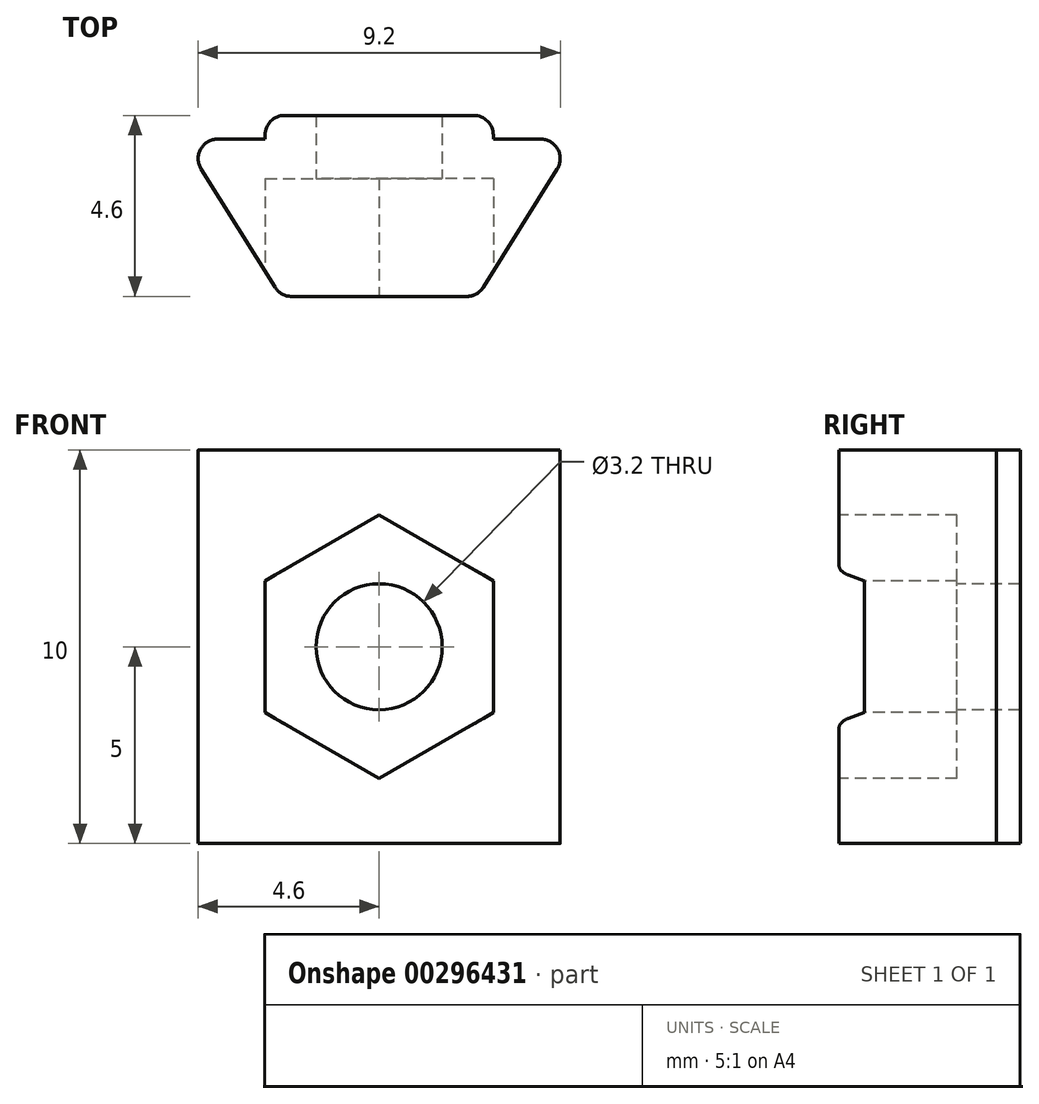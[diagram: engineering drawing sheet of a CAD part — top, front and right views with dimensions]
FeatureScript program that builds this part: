
annotation { "Feature Type Name" : "Feature", "Feature Type Description" : "" }
export const myFeature = defineFeature(function(context is Context, id is Id, definition is map)
    precondition{}
    {
        {
            var Q0;
            Q0=qCreatedBy(makeId("Top.planeOp"),FACE);
            var sketch = newSketch(context, id + "F0", { "sketchPlane" : qUnion([Q0])});
            skLineSegment(sketch, "E0.bottom", {"start": v(5, -2) * mm, "end": v(-5, -2) * mm, "construction": true});
            skLineSegment(sketch, "E0.top", {"start": v(5, 2) * mm, "end": v(-5, 2) * mm, "construction": true});
            skLineSegment(sketch, "E0.left", {"start": v(5, -2) * mm, "end": v(5, 2) * mm, "construction": true});
            skLineSegment(sketch, "E0.right", {"start": v(-5, -2) * mm, "end": v(-5, 2) * mm, "construction": true});
            skPoint(sketch, "E0.middle", {"position": v(0, 0) * mm});
            skLineSegment(sketch, "E1.bottom", {"start": v(2.9, 2.6) * mm, "end": v(-2.9, 2.6) * mm, "construction": true});
            skLineSegment(sketch, "E1.top", {"start": v(2.9, 1.4) * mm, "end": v(-2.9, 1.4) * mm, "construction": true});
            skLineSegment(sketch, "E1.left", {"start": v(2.9, 2.6) * mm, "end": v(2.9, 1.4) * mm, "construction": true});
            skLineSegment(sketch, "E1.right", {"start": v(-2.9, 2.6) * mm, "end": v(-2.9, 1.4) * mm, "construction": true});
            skPoint(sketch, "E1.middle", {"position": v(0, 2) * mm});
            skLineSegment(sketch, "E2", {"start": v(-5, 2) * mm, "end": v(-2.5, -2) * mm});
            skLineSegment(sketch, "E3", {"start": v(5, 2) * mm, "end": v(2.5, -2) * mm});
            skLineSegment(sketch, "E4", {"start": v(-2.5, -2) * mm, "end": v(2.5, -2) * mm});
            skLineSegment(sketch, "E5", {"start": v(-5, 2) * mm, "end": v(-2.9, 2) * mm});
            skLineSegment(sketch, "E6", {"start": v(-2.9, 2) * mm, "end": v(-2.9, 2.6) * mm});
            skLineSegment(sketch, "E7", {"start": v(-2.9, 2.6) * mm, "end": v(2.9, 2.6) * mm});
            skLineSegment(sketch, "E8", {"start": v(2.9, 2.6) * mm, "end": v(2.9, 2) * mm});
            skLineSegment(sketch, "E9", {"start": v(2.9, 2) * mm, "end": v(5, 2) * mm});
            skSolve(sketch);
        }
        {
            var Q0;
            Q0 = qSketchRegion(id + "F0", true);
            extrude(context, id + "F1", {"entities" : qUnion([Q0]), "depth" : 10 * mm});
        }
        {
            var Q0;
            Q0=makeQuery(id+"F1.opExtrude","SWEPT_FACE",FACE,{"disambiguationData":[OSD([sQuery(id+"F0.wireOp",EDGE,"E4")])]});
            var sketch = newSketch(context, id + "F2", { "sketchPlane" : qUnion([Q0])});
            skCircle(sketch, "E10.cCircle", {"center": v(0, 5) * mm, "radius": 2.9 * mm, "construction": true});
            skPoint(sketch, "E10.cCircle.centerSnap0", {"position": v(2.5, 5) * mm});
            skPoint(sketch, "E10.cCircle.centerSnap1", {"position": v(0, 10) * mm});
            skLineSegment(sketch, "E10.0", {"start": v(2.9, 3.33) * mm, "end": v(0, 1.65) * mm});
            skLineSegment(sketch, "E10.1", {"start": v(0, 1.65) * mm, "end": v(-2.9, 3.33) * mm});
            skLineSegment(sketch, "E10.2", {"start": v(-2.9, 3.33) * mm, "end": v(-2.9, 6.67) * mm});
            skLineSegment(sketch, "E10.3", {"start": v(-2.9, 6.67) * mm, "end": v(0, 8.35) * mm});
            skLineSegment(sketch, "E10.4", {"start": v(0, 8.35) * mm, "end": v(2.9, 6.67) * mm});
            skLineSegment(sketch, "E10.5", {"start": v(2.9, 6.67) * mm, "end": v(2.9, 3.33) * mm});
            skPoint(sketch, "E10.0.midPoint", {"position": v(1.45, 2.49) * mm});
            skCircle(sketch, "E11", {"center": v(0, 5) * mm, "radius": 1.6 * mm});
            skSolve(sketch);
        }
        {
            var Q0;
            Q0=makeQuery(id+"F2.imprint","IMPRINT",FACE,{"disambiguationData":[TD([[makeQuery(id+"F2.imprint","IMPRINT",EDGE,{"derivedFrom":sQuery(id+"F2.wireOp",EDGE,"E11")}),1.0]])]});
            extrude(context, id + "F3", {"entities" : qUnion([Q0]), "operationType" : NewBodyOperationType.REMOVE, "endBound" : BoundingType.THROUGH_ALL, "oppositeDirection" : true, "depth" : 25 * mm});
        }
        {
            var Q0;
            Q0=makeQuery(id+"F2.imprint","IMPRINT",FACE,{"disambiguationData":[TD([[makeQuery(id+"F2.imprint","IMPRINT",EDGE,{"derivedFrom":sQuery(id+"F2.wireOp",EDGE,"E11")}),-1.0]])]});
            var Q1;
            {var subQ0=sQuery(id+"F2.wireOp",EDGE,"E10.5");Q1=makeQuery(id+"F2.imprint","IMPRINT",FACE,{"disambiguationData":[TD([[makeQuery(id+"F2.imprint","IMPRINT",EDGE,{"derivedFrom":subQ0}),-1.0]])]});}
            var Q2;
            {var subQ0=sQuery(id+"F2.wireOp",EDGE,"E10.2");Q2=makeQuery(id+"F2.imprint","IMPRINT",FACE,{"disambiguationData":[TD([[makeQuery(id+"F2.imprint","IMPRINT",EDGE,{"derivedFrom":subQ0}),-1.0]])]});}
            extrude(context, id + "F4", {"entities" : qUnion([Q0, Q1, Q2]), "operationType" : NewBodyOperationType.REMOVE, "oppositeDirection" : true, "depth" : 3 * mm});
        }
        {
            var Q0;
            Q0=makeQuery(id+"F1.opExtrude","SWEPT_EDGE",EDGE,{"disambiguationData":[OSD([sQuery(id+"F0.wireOp",EDGE,"E2"),sQuery(id+"F0.wireOp",EDGE,"E5")])]});
            var Q1;
            {var subQ0=sQuery(id+"F0.wireOp",EDGE,"E2");var subQ1=sQuery(id+"F0.wireOp",EDGE,"E4");Q1=makeQuery(id+"F4.boolean.opBoolean","SPLIT",EDGE,{"disambiguationData":[TD([makeQuery(id+"F4.opExtrude","SWEPT_FACE",FACE,{"disambiguationData":[OSD([sQuery(id+"F2.wireOp",EDGE,"E10.3")])]})])],"derivedFrom":makeQuery(id+"F1.opExtrude","SWEPT_EDGE",EDGE,{"disambiguationData":[OSD([subQ0,subQ1])]})});}
            var Q2;
            {var subQ0=sQuery(id+"F0.wireOp",EDGE,"E2");var subQ1=sQuery(id+"F0.wireOp",EDGE,"E4");Q2=makeQuery(id+"F4.boolean.opBoolean","SPLIT",EDGE,{"disambiguationData":[TD([makeQuery(id+"F4.opExtrude","SWEPT_FACE",FACE,{"disambiguationData":[OSD([sQuery(id+"F2.wireOp",EDGE,"E10.1")])]})])],"derivedFrom":makeQuery(id+"F1.opExtrude","SWEPT_EDGE",EDGE,{"disambiguationData":[OSD([subQ0,subQ1])]})});}
            var Q3;
            {var subQ0=sQuery(id+"F0.wireOp",EDGE,"E4");var subQ1=sQuery(id+"F0.wireOp",EDGE,"E3");Q3=makeQuery(id+"F4.boolean.opBoolean","SPLIT",EDGE,{"disambiguationData":[TD([makeQuery(id+"F4.opExtrude","SWEPT_FACE",FACE,{"disambiguationData":[OSD([sQuery(id+"F2.wireOp",EDGE,"E10.4")])]})])],"derivedFrom":makeQuery(id+"F1.opExtrude","SWEPT_EDGE",EDGE,{"disambiguationData":[OSD([subQ1,subQ0])]})});}
            var Q4;
            {var subQ0=sQuery(id+"F0.wireOp",EDGE,"E4");var subQ1=sQuery(id+"F0.wireOp",EDGE,"E3");Q4=makeQuery(id+"F4.boolean.opBoolean","SPLIT",EDGE,{"disambiguationData":[TD([makeQuery(id+"F4.opExtrude","SWEPT_FACE",FACE,{"disambiguationData":[OSD([sQuery(id+"F2.wireOp",EDGE,"E10.0")])]})])],"derivedFrom":makeQuery(id+"F1.opExtrude","SWEPT_EDGE",EDGE,{"disambiguationData":[OSD([subQ1,subQ0])]})});}
            var Q5;
            Q5=makeQuery(id+"F1.opExtrude","SWEPT_EDGE",EDGE,{"disambiguationData":[OSD([sQuery(id+"F0.wireOp",EDGE,"E3"),sQuery(id+"F0.wireOp",EDGE,"E9")])]});
            var Q6;
            Q6=makeQuery(id+"F1.opExtrude","SWEPT_EDGE",EDGE,{"disambiguationData":[OSD([sQuery(id+"F0.wireOp",EDGE,"E6"),sQuery(id+"F0.wireOp",EDGE,"E7")])]});
            var Q7;
            Q7=makeQuery(id+"F1.opExtrude","SWEPT_EDGE",EDGE,{"disambiguationData":[OSD([sQuery(id+"F0.wireOp",EDGE,"E7"),sQuery(id+"F0.wireOp",EDGE,"E8")])]});
            fillet(context, id + "F5", {"entities" : qUnion([Q0, Q1, Q2, Q3, Q4, Q5, Q6, Q7]), "radius" : 0.5 * mm, "tangentPropagation" : true, "allowEdgeOverflow" : false});
        }
    });
